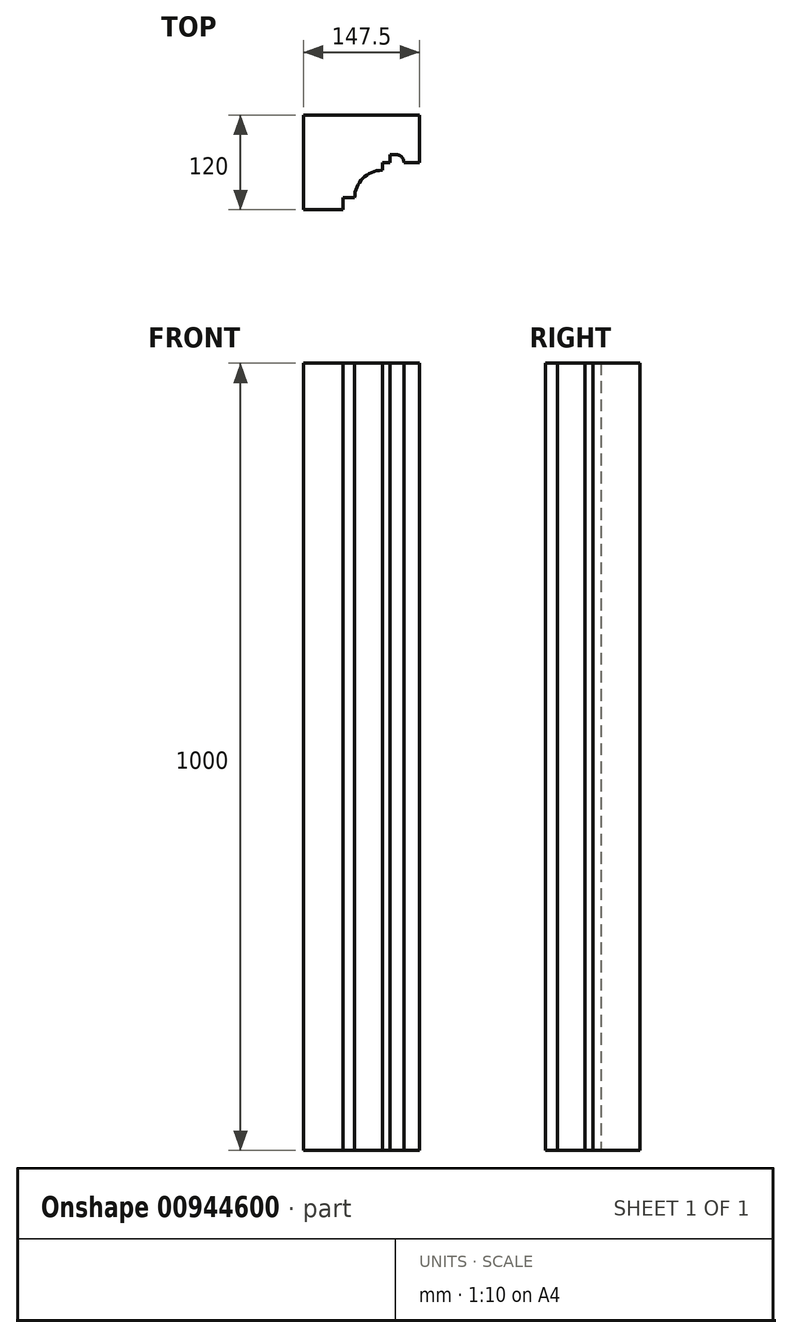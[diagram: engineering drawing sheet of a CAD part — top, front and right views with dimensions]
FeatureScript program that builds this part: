
annotation { "Feature Type Name" : "Feature", "Feature Type Description" : "" }
export const myFeature = defineFeature(function(context is Context, id is Id, definition is map)
    precondition{}
    {
        {
            var Q0;
            Q0=qCreatedBy(makeId("Top.planeOp"),FACE);
            var sketch = newSketch(context, id + "F0", { "sketchPlane" : qUnion([Q0])});
            skLineSegment(sketch, "E0", {"start": v(51.77, 165.7) * mm, "end": v(-95.73, 165.7) * mm});
            skLineSegment(sketch, "E1", {"start": v(-95.73, 165.7) * mm, "end": v(-95.73, 45.7) * mm});
            skLineSegment(sketch, "E2", {"start": v(51.77, 165.7) * mm, "end": v(51.77, 105.7) * mm});
            skLineSegment(sketch, "E3", {"start": v(51.77, 105.7) * mm, "end": v(31.77, 105.7) * mm});
            skPoint(sketch, "E4", {"position": v(21.77, 105.7) * mm});
            skArc(sketch, "E5", {"start": v(31.77, 105.7) * mm, "mid": v(28.84, 112.77) * mm, "end": v(21.77, 115.7) * mm});
            skLineSegment(sketch, "E6", {"start": v(21.77, 115.7) * mm, "end": v(14.27, 115.7) * mm});
            skLineSegment(sketch, "E7", {"start": v(14.27, 115.7) * mm, "end": v(14.27, 105.7) * mm});
            skLineSegment(sketch, "E8", {"start": v(14.27, 105.7) * mm, "end": v(4.27, 105.7) * mm});
            skLineSegment(sketch, "E9", {"start": v(4.27, 105.7) * mm, "end": v(4.27, 95.7) * mm});
            skArc(sketch, "E10", {"start": v(4.27, 95.7) * mm, "mid": v(-20.48, 85.45) * mm, "end": v(-30.73, 60.7) * mm});
            skLineSegment(sketch, "E11", {"start": v(-30.73, 60.7) * mm, "end": v(-45.73, 60.7) * mm});
            skLineSegment(sketch, "E12", {"start": v(-45.73, 60.7) * mm, "end": v(-45.73, 45.7) * mm});
            skLineSegment(sketch, "E13", {"start": v(-45.73, 45.7) * mm, "end": v(-95.73, 45.7) * mm});
            skSolve(sketch);
        }
        {
            var Q0;
            Q0 = qSketchRegion(id + "F0", true);
            extrude(context, id + "F1", {"entities" : qUnion([Q0]), "depth" : 1000 * mm, "offsetDistance" : 25 * mm});
        }
    });
